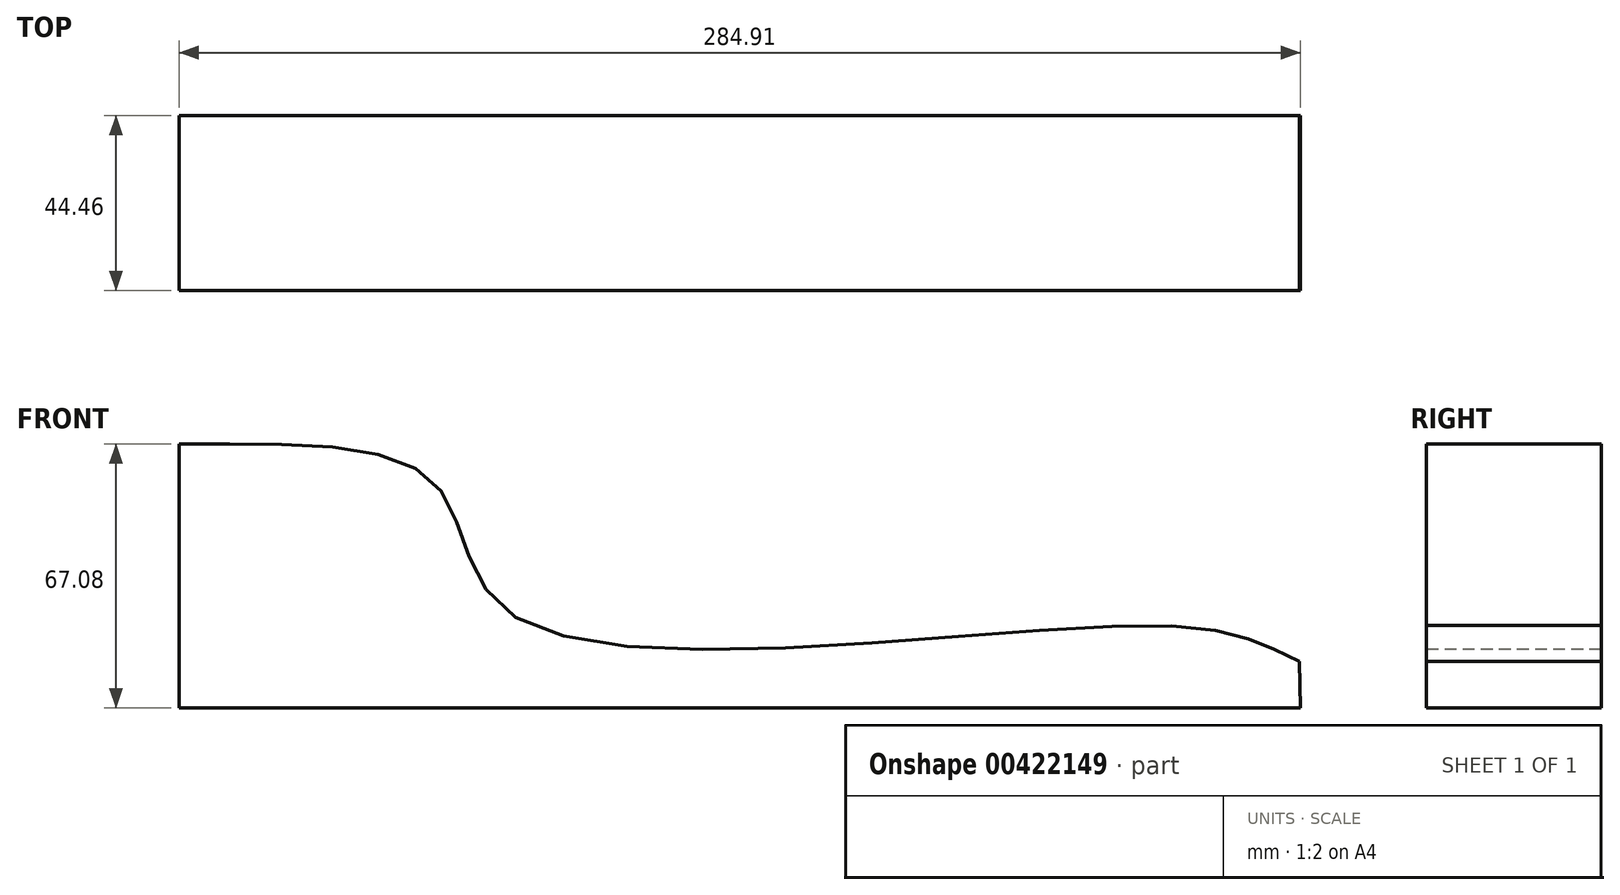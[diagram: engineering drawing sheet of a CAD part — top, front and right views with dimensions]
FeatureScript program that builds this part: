
annotation { "Feature Type Name" : "Feature", "Feature Type Description" : "" }
export const myFeature = defineFeature(function(context is Context, id is Id, definition is map)
    precondition{}
    {
        {
            var Q0;
            Q0=qCreatedBy(makeId("Front.planeOp"),FACE);
            var sketch = newSketch(context, id + "F0", { "sketchPlane" : qUnion([Q0])});
            skLineSegment(sketch, "E0.top", {"start": v(-145.45, -20.68) * mm, "end": v(139.46, -20.68) * mm});
            skLineSegment(sketch, "E0.left", {"start": v(-145.45, 46.4) * mm, "end": v(-145.45, -20.68) * mm});
            skLineSegment(sketch, "E1", {"start": v(139.22, -8.79) * mm, "end": v(139.46, -20.68) * mm});
            skFitSpline(sketch, "E2", {"points": [v(-145.45, 46.4) * mm, v(-81.16, 37.17) * mm, v(-59.8, 2.28) * mm, v(105.48, 0.21) * mm, v(139.22, -8.79) * mm], "startDerivative": vector(282.95, -3.95) * mm, "endDerivative": vector(150, -68.82) * mm});
            skSolve(sketch);
        }
        {
            var Q0;
            Q0=makeQuery(id+"F0.imprint","IMPRINT",FACE,{"disambiguationData":[TD([[makeQuery(id+"F0.imprint","IMPRINT",EDGE,{"derivedFrom":sQuery(id+"F0.wireOp",EDGE,"E0.top")}),1.0]])]});
            extrude(context, id + "F1", {"entities" : qUnion([Q0]), "depth" : 44.45 * mm, "symmetric" : true});
        }
    });
